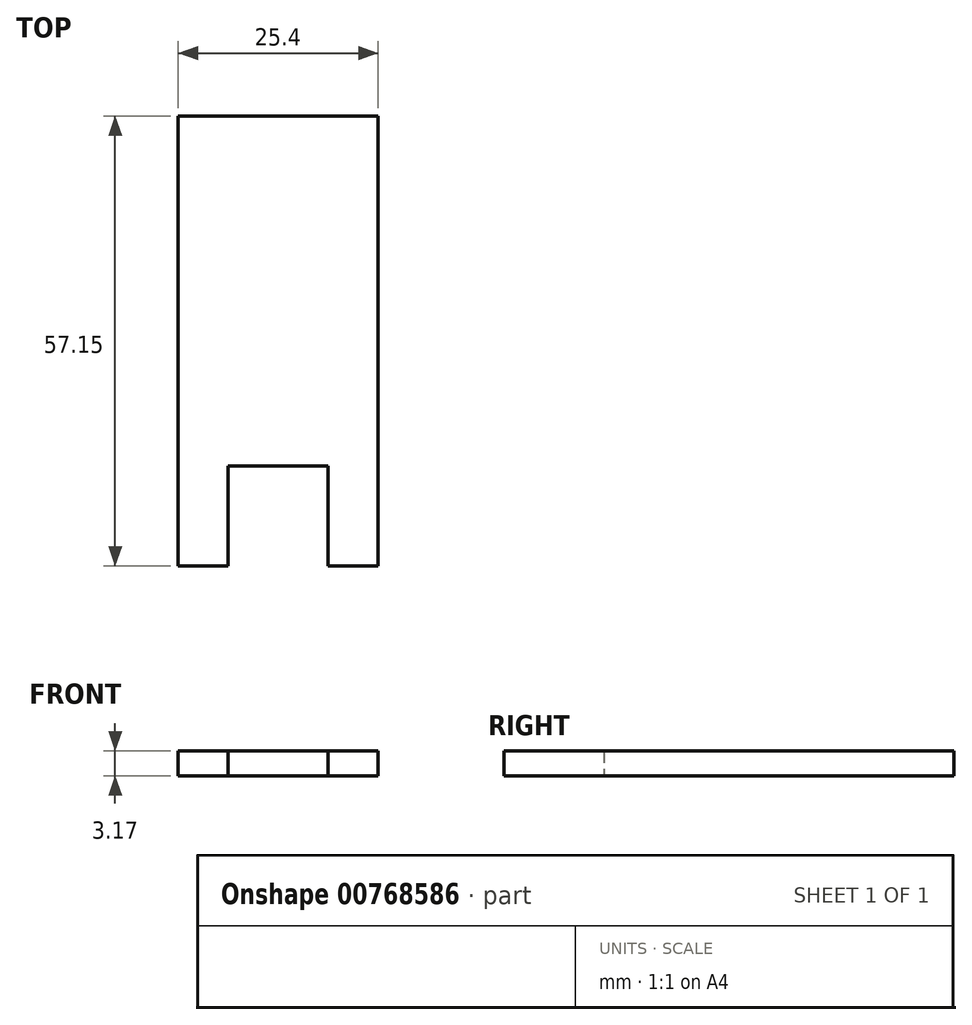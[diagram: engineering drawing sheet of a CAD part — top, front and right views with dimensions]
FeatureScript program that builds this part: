
annotation { "Feature Type Name" : "Feature", "Feature Type Description" : "" }
export const myFeature = defineFeature(function(context is Context, id is Id, definition is map)
    precondition{}
    {
        {
            var Q0;
            Q0=qCreatedBy(makeId("Top.planeOp"),FACE);
            var sketch = newSketch(context, id + "F0", { "sketchPlane" : qUnion([Q0])});
            skLineSegment(sketch, "E0", {"start": v(-12.7, 0) * mm, "end": v(-12.7, 57.15) * mm});
            skLineSegment(sketch, "E1", {"start": v(12.7, 0) * mm, "end": v(12.7, 57.15) * mm});
            skLineSegment(sketch, "E2", {"start": v(-12.7, 57.15) * mm, "end": v(12.7, 57.15) * mm});
            skLineSegment(sketch, "E3", {"start": v(-12.7, 0) * mm, "end": v(12.7, 0) * mm});
            skPoint(sketch, "E4", {"position": v(0, 0) * mm});
            skLineSegment(sketch, "E5", {"start": v(-6.35, 0) * mm, "end": v(-6.35, 12.7) * mm});
            skLineSegment(sketch, "E6", {"start": v(-6.35, 12.7) * mm, "end": v(6.35, 12.7) * mm});
            skLineSegment(sketch, "E7", {"start": v(6.35, 12.7) * mm, "end": v(6.35, 0) * mm});
            skSolve(sketch);
        }
        {
            var Q0;
            Q0=makeQuery(id+"F0.imprint","IMPRINT",FACE,{"disambiguationData":[TD([[makeQuery(id+"F0.imprint","IMPRINT",EDGE,{"derivedFrom":sQuery(id+"F0.wireOp",EDGE,"E0")}),-1.0]])]});
            extrude(context, id + "F1", {"entities" : qUnion([Q0]), "depth" : 3.17 * mm, "offsetDistance" : 25.4 * mm});
        }
    });
